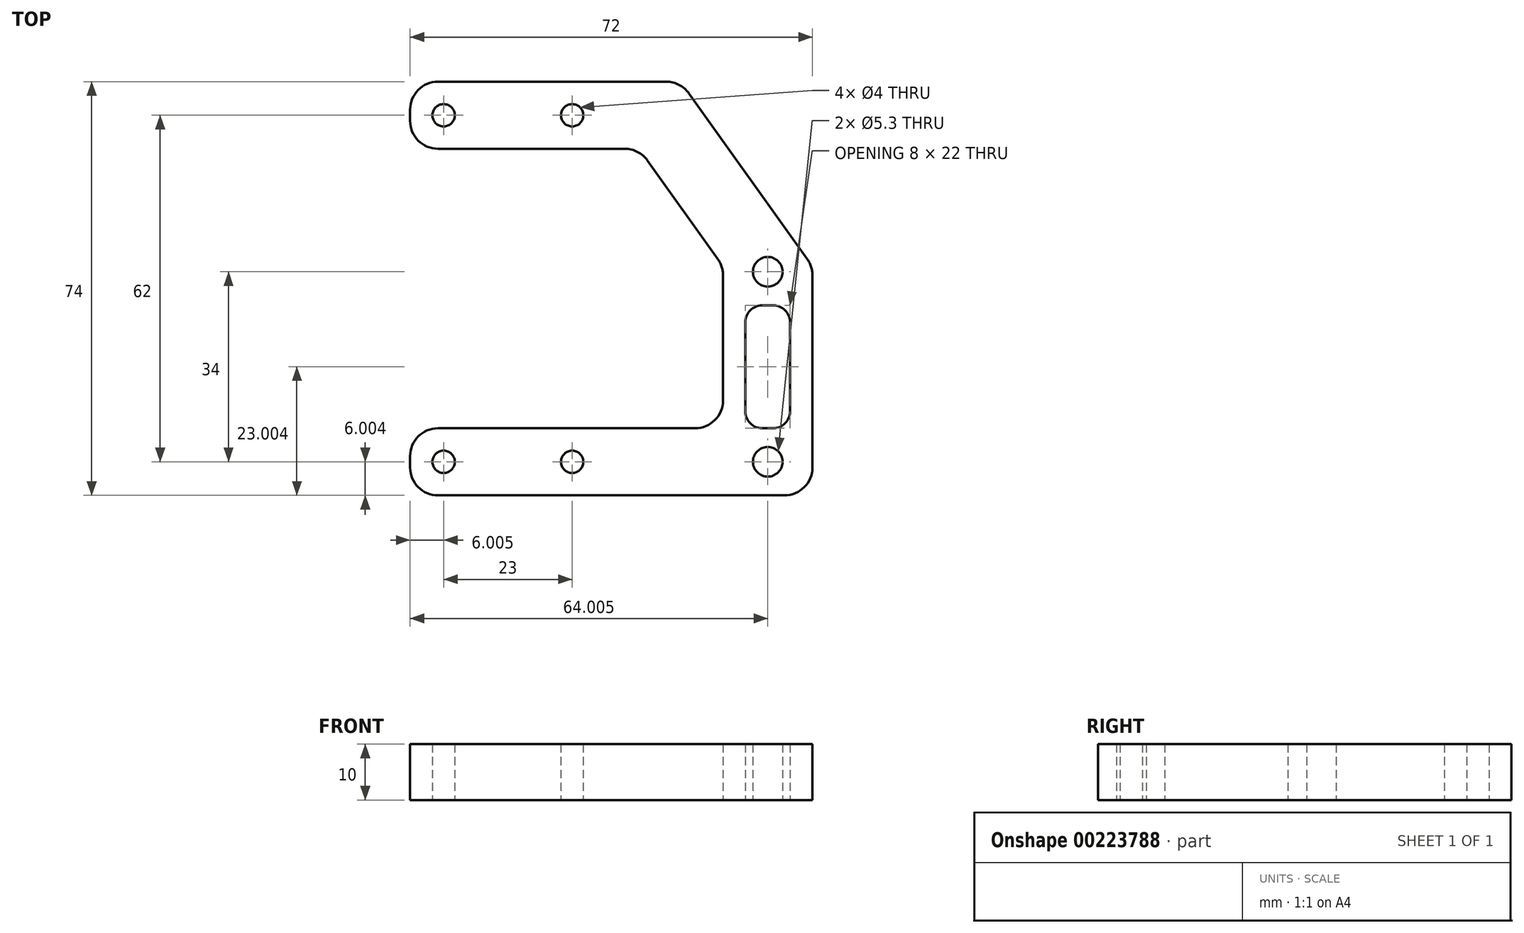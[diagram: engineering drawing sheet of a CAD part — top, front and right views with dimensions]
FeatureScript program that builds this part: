
annotation { "Feature Type Name" : "Feature", "Feature Type Description" : "" }
export const myFeature = defineFeature(function(context is Context, id is Id, definition is map)
    precondition{}
    {
        {
            var Q0;
            Q0=qCreatedBy(makeId("Top.planeOp"),FACE);
            var sketch = newSketch(context, id + "F0", { "sketchPlane" : qUnion([Q0])});
            skCircle(sketch, "E0", {"center": v(53.96, 29.9) * mm, "radius": 2.65 * mm});
            skCircle(sketch, "E1", {"center": v(53.96, -4.1) * mm, "radius": 2.65 * mm});
            skCircle(sketch, "E2", {"center": v(18.96, -4.1) * mm, "radius": 2 * mm});
            skCircle(sketch, "E3", {"center": v(-4.04, -4.1) * mm, "radius": 2 * mm});
            skLineSegment(sketch, "E4.top", {"start": v(56.96, -10.1) * mm, "end": v(-5.04, -10.1) * mm});
            skLineSegment(sketch, "E4.left", {"start": v(61.96, 29.3) * mm, "end": v(61.96, -5.1) * mm});
            skLineSegment(sketch, "E4.right", {"start": v(-10.04, -3.1) * mm, "end": v(-10.04, -5.1) * mm});
            skLineSegment(sketch, "E5", {"start": v(45.96, 29.3) * mm, "end": v(45.96, 6.9) * mm});
            skLineSegment(sketch, "E6", {"start": v(40.96, 1.9) * mm, "end": v(-5.04, 1.9) * mm});
            skLineSegment(sketch, "E7.bottom", {"start": v(52.96, 23.9) * mm, "end": v(54.96, 23.9) * mm});
            skLineSegment(sketch, "E7.top", {"start": v(52.96, 1.9) * mm, "end": v(54.96, 1.9) * mm});
            skLineSegment(sketch, "E7.left", {"start": v(49.96, 20.9) * mm, "end": v(49.96, 4.9) * mm});
            skLineSegment(sketch, "E7.right", {"start": v(57.96, 20.9) * mm, "end": v(57.96, 4.9) * mm});
            skPoint(sketch, "E8.visualSharp", {"position": v(-10.04, 1.9) * mm});
            skArc(sketch, "E8.filletArc", {"start": v(-5.04, 1.9) * mm, "mid": v(-8.57, 0.43) * mm, "end": v(-10.04, -3.1) * mm});
            skPoint(sketch, "E9.visualSharp", {"position": v(-10.04, -10.1) * mm});
            skArc(sketch, "E9.filletArc", {"start": v(-10.04, -5.1) * mm, "mid": v(-8.57, -8.64) * mm, "end": v(-5.04, -10.1) * mm});
            skPoint(sketch, "E10.visualSharp", {"position": v(61.96, -10.1) * mm});
            skArc(sketch, "E10.filletArc", {"start": v(56.96, -10.1) * mm, "mid": v(60.5, -8.64) * mm, "end": v(61.96, -5.1) * mm});
            skPoint(sketch, "E11.visualSharp", {"position": v(61.96, 35.9) * mm});
            skPoint(sketch, "E12.visualSharp", {"position": v(45.96, 35.9) * mm});
            skPoint(sketch, "E13.visualSharp", {"position": v(45.96, 1.9) * mm});
            skArc(sketch, "E13.filletArc", {"start": v(40.96, 1.9) * mm, "mid": v(44.5, 3.36) * mm, "end": v(45.96, 6.9) * mm});
            skPoint(sketch, "E14.visualSharp", {"position": v(49.96, 1.9) * mm});
            skArc(sketch, "E14.filletArc", {"start": v(49.96, 4.9) * mm, "mid": v(50.84, 2.77) * mm, "end": v(52.96, 1.9) * mm});
            skPoint(sketch, "E15.visualSharp", {"position": v(57.96, 23.9) * mm});
            skArc(sketch, "E15.filletArc", {"start": v(57.96, 20.9) * mm, "mid": v(57.09, 23.02) * mm, "end": v(54.96, 23.9) * mm});
            skPoint(sketch, "E16.visualSharp", {"position": v(49.96, 23.9) * mm});
            skArc(sketch, "E16.filletArc", {"start": v(52.96, 23.9) * mm, "mid": v(50.84, 23.02) * mm, "end": v(49.96, 20.9) * mm});
            skPoint(sketch, "E17.visualSharp", {"position": v(57.96, 1.9) * mm});
            skArc(sketch, "E17.filletArc", {"start": v(54.96, 1.9) * mm, "mid": v(57.09, 2.77) * mm, "end": v(57.96, 4.9) * mm});
            skCircle(sketch, "E18", {"center": v(-4.04, 57.9) * mm, "radius": 2 * mm});
            skCircle(sketch, "E19", {"center": v(18.96, 57.9) * mm, "radius": 2 * mm});
            skLineSegment(sketch, "E20", {"start": v(-10.04, 58.9) * mm, "end": v(-10.04, 56.9) * mm});
            skLineSegment(sketch, "E21", {"start": v(-5.04, 51.9) * mm, "end": v(28.4, 51.9) * mm});
            skLineSegment(sketch, "E22", {"start": v(32.46, 49.8) * mm, "end": v(45.03, 32.2) * mm});
            skPoint(sketch, "E23.start.orphan", {"position": v(30.96, 63.9) * mm});
            skLineSegment(sketch, "E24", {"start": v(61.03, 32.2) * mm, "end": v(39.89, 61.8) * mm});
            skLineSegment(sketch, "E25", {"start": v(35.82, 63.9) * mm, "end": v(-5.04, 63.9) * mm});
            skPoint(sketch, "E26.visualSharp", {"position": v(-10.04, 51.9) * mm});
            skArc(sketch, "E26.filletArc", {"start": v(-10.04, 56.9) * mm, "mid": v(-8.57, 53.36) * mm, "end": v(-5.04, 51.9) * mm});
            skPoint(sketch, "E27.visualSharp", {"position": v(-10.04, 63.9) * mm});
            skArc(sketch, "E27.filletArc", {"start": v(-5.04, 63.9) * mm, "mid": v(-8.57, 62.43) * mm, "end": v(-10.04, 58.9) * mm});
            skPoint(sketch, "E28.visualSharp", {"position": v(38.4, 63.9) * mm});
            skArc(sketch, "E28.filletArc", {"start": v(39.89, 61.8) * mm, "mid": v(38.1, 63.34) * mm, "end": v(35.82, 63.9) * mm});
            skPoint(sketch, "E29.visualSharp", {"position": v(30.96, 51.9) * mm});
            skArc(sketch, "E29.filletArc", {"start": v(32.46, 49.8) * mm, "mid": v(30.68, 51.34) * mm, "end": v(28.4, 51.9) * mm});
            skPoint(sketch, "E30.visualSharp", {"position": v(45.96, 30.9) * mm});
            skArc(sketch, "E30.filletArc", {"start": v(45.96, 29.3) * mm, "mid": v(45.73, 30.82) * mm, "end": v(45.03, 32.2) * mm});
            skPoint(sketch, "E31.visualSharp", {"position": v(61.96, 30.9) * mm});
            skArc(sketch, "E31.filletArc", {"start": v(61.96, 29.3) * mm, "mid": v(61.73, 30.82) * mm, "end": v(61.03, 32.2) * mm});
            skSolve(sketch);
        }
        {
            var Q0;
            Q0 = qSketchRegion(id + "F0", true);
            var Q1;
            Q1=makeQuery(id+"F0.imprint","IMPRINT",FACE,{"disambiguationData":[TD([[makeQuery(id+"F0.imprint","IMPRINT",EDGE,{"derivedFrom":sQuery(id+"F0.wireOp",EDGE,"E0")}),-1.0]])]});
            extrude(context, id + "F1", {"entities" : qUnion([Q0, Q1]), "depth" : 10 * mm});
        }
    });
